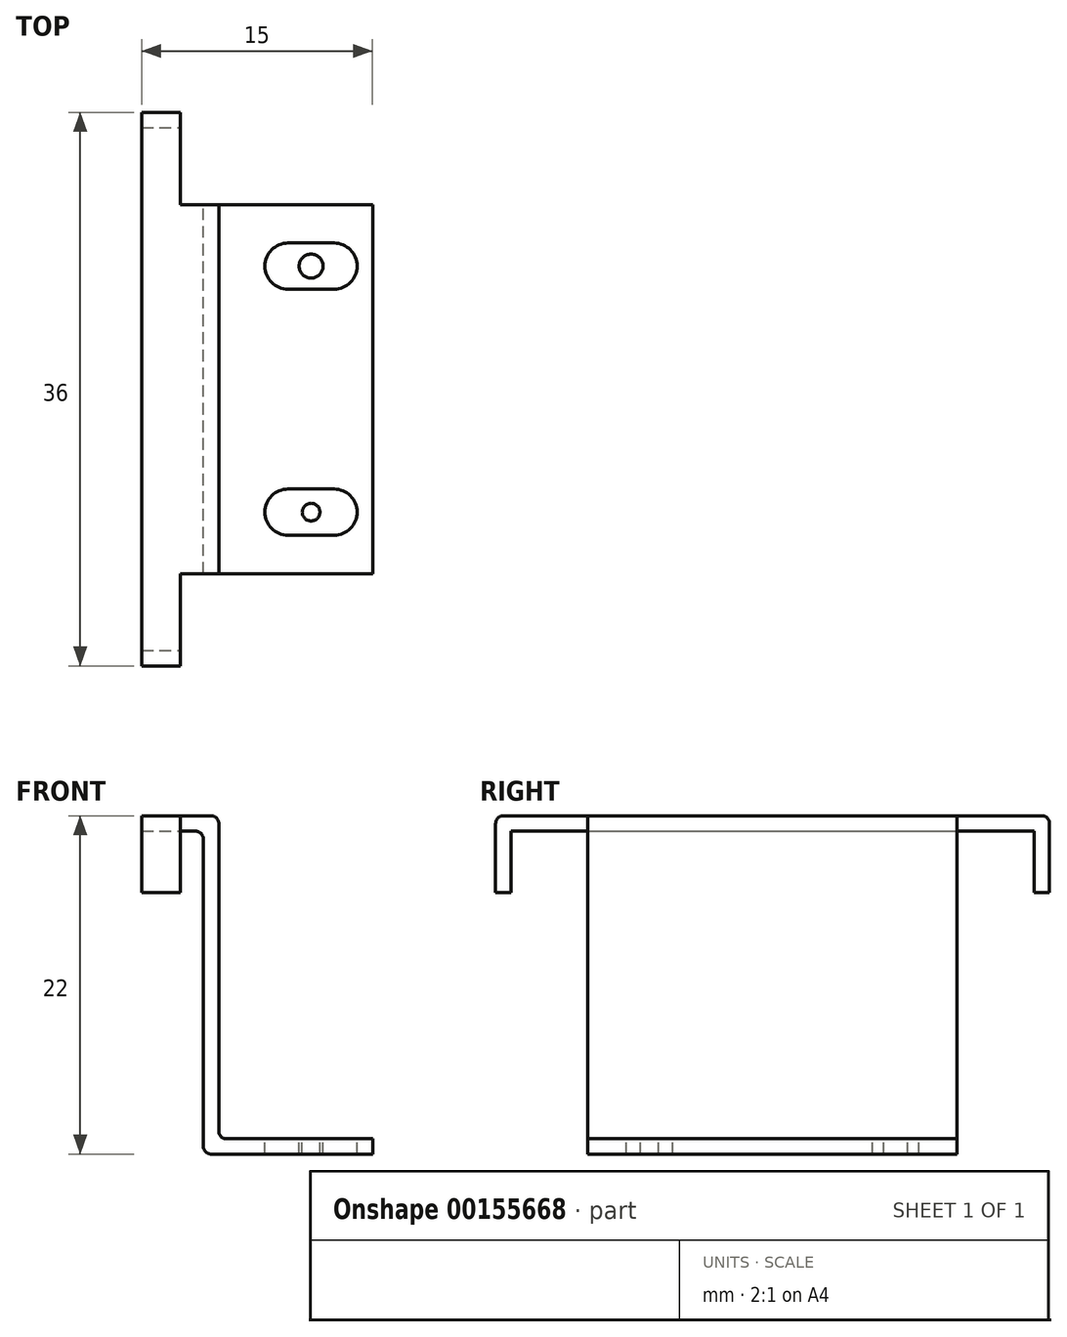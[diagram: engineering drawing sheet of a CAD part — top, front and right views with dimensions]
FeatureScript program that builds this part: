
annotation { "Feature Type Name" : "Feature", "Feature Type Description" : "" }
export const myFeature = defineFeature(function(context is Context, id is Id, definition is map)
    precondition{}
    {
        {
            var Q0;
            Q0=qCreatedBy(makeId("Front.planeOp"),FACE);
            var sketch = newSketch(context, id + "F0", { "sketchPlane" : qUnion([Q0])});
            skLineSegment(sketch, "E0.bottom", {"start": v(47.04, 40.35) * mm, "end": v(57.04, 40.35) * mm});
            skLineSegment(sketch, "E0.top", {"start": v(46.04, 39.35) * mm, "end": v(57.04, 39.35) * mm});
            skLineSegment(sketch, "E0.right", {"start": v(57.04, 40.35) * mm, "end": v(57.04, 39.35) * mm});
            skLineSegment(sketch, "E1.left", {"start": v(47.04, 40.35) * mm, "end": v(47.04, 61.35) * mm});
            skLineSegment(sketch, "E1.right", {"start": v(46.04, 39.35) * mm, "end": v(46.04, 60.35) * mm});
            skLineSegment(sketch, "E2.bottom", {"start": v(46.04, 60.35) * mm, "end": v(42.04, 60.35) * mm});
            skLineSegment(sketch, "E2.top", {"start": v(47.04, 61.35) * mm, "end": v(42.04, 61.35) * mm});
            skLineSegment(sketch, "E2.right", {"start": v(42.04, 60.35) * mm, "end": v(42.04, 61.35) * mm});
            skSolve(sketch);
        }
        {
            var Q0;
            Q0 = qSketchRegion(id + "F0", true);
            extrude(context, id + "F1", {"entities" : qUnion([Q0]), "depth" : 24 * mm});
        }
        {
            var Q0;
            Q0=makeQuery(id+"F1.opExtrude","SWEPT_FACE",FACE,{"disambiguationData":[OSD([sQuery(id+"F0.wireOp",EDGE,"E2.top")])]});
            var sketch = newSketch(context, id + "F2", { "sketchPlane" : qUnion([Q0])});
            skPoint(sketch, "E3.oppositeSnap0", {"position": v(44.54, -24) * mm});
            skLineSegment(sketch, "E3.bottom", {"start": v(42.04, -24) * mm, "end": v(44.54, -24) * mm});
            skLineSegment(sketch, "E3.top", {"start": v(42.04, -30) * mm, "end": v(44.54, -30) * mm});
            skLineSegment(sketch, "E3.left", {"start": v(42.04, -24) * mm, "end": v(42.04, -30) * mm});
            skLineSegment(sketch, "E3.right", {"start": v(44.54, -24) * mm, "end": v(44.54, -30) * mm});
            skPoint(sketch, "E4.oppositeSnap0", {"position": v(44.54, 0) * mm});
            skLineSegment(sketch, "E4.bottom", {"start": v(42.04, 0) * mm, "end": v(44.54, 0) * mm});
            skLineSegment(sketch, "E4.top", {"start": v(42.04, 6) * mm, "end": v(44.54, 6) * mm});
            skLineSegment(sketch, "E4.left", {"start": v(42.04, 0) * mm, "end": v(42.04, 6) * mm});
            skLineSegment(sketch, "E4.right", {"start": v(44.54, 0) * mm, "end": v(44.54, 6) * mm});
            skSolve(sketch);
        }
        {
            var Q0;
            Q0 = qSketchRegion(id + "F2", true);
            extrude(context, id + "F3", {"entities" : qUnion([Q0]), "operationType" : NewBodyOperationType.ADD, "oppositeDirection" : true, "depth" : 1 * mm});
        }
        {
            var Q0;
            Q0=makeQuery(id+"F3.boolean.opBoolean","MERGE",FACE,{"derivedFrom":[makeQuery(id+"F1.opExtrude","SWEPT_FACE",FACE,{"disambiguationData":[OSD([sQuery(id+"F0.wireOp",EDGE,"E2.bottom")])]}),makeQuery(id+"F3.opExtrude","CAP_FACE",FACE,{"disambiguationData":[OSD([sQuery(id+"F2.wireOp",EDGE,"E3.bottom"),sQuery(id+"F2.wireOp",EDGE,"E3.top"),sQuery(id+"F2.wireOp",EDGE,"E3.left"),sQuery(id+"F2.wireOp",EDGE,"E3.right")])],"isStart":false}),makeQuery(id+"F3.opExtrude","CAP_FACE",FACE,{"disambiguationData":[OSD([sQuery(id+"F2.wireOp",EDGE,"E4.bottom"),sQuery(id+"F2.wireOp",EDGE,"E4.top"),sQuery(id+"F2.wireOp",EDGE,"E4.left"),sQuery(id+"F2.wireOp",EDGE,"E4.right")])],"isStart":false})]});
            var sketch = newSketch(context, id + "F4", { "sketchPlane" : qUnion([Q0])});
            skLineSegment(sketch, "E5.bottom", {"start": v(42.04, -6) * mm, "end": v(44.54, -6) * mm});
            skLineSegment(sketch, "E5.top", {"start": v(42.04, -5) * mm, "end": v(44.54, -5) * mm});
            skLineSegment(sketch, "E5.left", {"start": v(42.04, -6) * mm, "end": v(42.04, -5) * mm});
            skLineSegment(sketch, "E5.right", {"start": v(44.54, -6) * mm, "end": v(44.54, -5) * mm});
            skLineSegment(sketch, "E6.bottom", {"start": v(42.04, 30) * mm, "end": v(44.54, 30) * mm});
            skLineSegment(sketch, "E6.top", {"start": v(42.04, 29) * mm, "end": v(44.54, 29) * mm});
            skLineSegment(sketch, "E6.left", {"start": v(42.04, 30) * mm, "end": v(42.04, 29) * mm});
            skLineSegment(sketch, "E6.right", {"start": v(44.54, 30) * mm, "end": v(44.54, 29) * mm});
            skSolve(sketch);
        }
        {
            var Q0;
            Q0 = qSketchRegion(id + "F4", true);
            extrude(context, id + "F5", {"entities" : qUnion([Q0]), "operationType" : NewBodyOperationType.ADD, "depth" : 4 * mm});
        }
        {
            var Q0;
            Q0=makeQuery(id+"F1.opExtrude","SWEPT_EDGE",EDGE,{"disambiguationData":[OSD([sQuery(id+"F0.wireOp",EDGE,"E0.bottom"),sQuery(id+"F0.wireOp",EDGE,"E1.left")])]});
            var Q1;
            Q1=makeQuery(id+"F1.opExtrude","SWEPT_EDGE",EDGE,{"disambiguationData":[OSD([sQuery(id+"F0.wireOp",EDGE,"E0.top"),sQuery(id+"F0.wireOp",EDGE,"E1.right")])]});
            var Q2;
            Q2=makeQuery(id+"F1.opExtrude","SWEPT_EDGE",EDGE,{"disambiguationData":[OSD([sQuery(id+"F0.wireOp",EDGE,"E1.left"),sQuery(id+"F0.wireOp",EDGE,"E2.top")])]});
            var Q3;
            Q3=makeQuery(id+"F1.opExtrude","SWEPT_EDGE",EDGE,{"disambiguationData":[OSD([sQuery(id+"F0.wireOp",EDGE,"E1.right"),sQuery(id+"F0.wireOp",EDGE,"E2.bottom")])]});
            var Q4;
            Q4=makeQuery(id+"F5.opExtrude","CAP_EDGE",EDGE,{"disambiguationData":[OSD([sQuery(id+"F4.wireOp",EDGE,"E5.top")])],"isStart":true});
            var Q5;
            Q5=makeQuery(id+"F5.opExtrude","CAP_EDGE",EDGE,{"disambiguationData":[OSD([sQuery(id+"F4.wireOp",EDGE,"E6.top")])],"isStart":true});
            var Q6;
            Q6=makeQuery(id+"F3.opExtrude","CAP_EDGE",EDGE,{"disambiguationData":[OSD([sQuery(id+"F2.wireOp",EDGE,"E4.top")])],"isStart":true});
            var Q7;
            Q7=makeQuery(id+"F3.opExtrude","CAP_EDGE",EDGE,{"disambiguationData":[OSD([sQuery(id+"F2.wireOp",EDGE,"E3.top")])],"isStart":true});
            fillet(context, id + "F6", {"entities" : qUnion([Q0, Q1, Q2, Q3, Q4, Q5, Q6, Q7]), "radius" : 0.5 * mm, "tangentPropagation" : true, "allowEdgeOverflow" : false});
        }
        {
            var Q0;
            Q0=makeQuery(id+"F1.opExtrude","SWEPT_FACE",FACE,{"disambiguationData":[OSD([sQuery(id+"F0.wireOp",EDGE,"E0.bottom")])]});
            var sketch = newSketch(context, id + "F7", { "sketchPlane" : qUnion([Q0])});
            skLineSegment(sketch, "E7.bottom", {"start": v(54.54, -18.5) * mm, "end": v(51.54, -18.5) * mm});
            skLineSegment(sketch, "E7.top", {"start": v(54.54, -21.5) * mm, "end": v(51.54, -21.5) * mm});
            skPoint(sketch, "E7.middle", {"position": v(53.04, -20) * mm});
            skArc(sketch, "E8", {"start": v(51.54, -21.5) * mm, "mid": v(50.04, -20) * mm, "end": v(51.54, -18.5) * mm});
            skArc(sketch, "E9", {"start": v(54.54, -21.5) * mm, "mid": v(56.04, -20) * mm, "end": v(54.54, -18.5) * mm});
            skLineSegment(sketch, "E10.bottom", {"start": v(54.54, -2.5) * mm, "end": v(51.54, -2.5) * mm});
            skLineSegment(sketch, "E10.top", {"start": v(54.54, -5.5) * mm, "end": v(51.54, -5.5) * mm});
            skPoint(sketch, "E10.middle", {"position": v(53.04, -4) * mm});
            skArc(sketch, "E11", {"start": v(51.54, -5.5) * mm, "mid": v(50.04, -4) * mm, "end": v(51.54, -2.5) * mm});
            skArc(sketch, "E12", {"start": v(54.54, -5.5) * mm, "mid": v(56.04, -4) * mm, "end": v(54.54, -2.5) * mm});
            skCircle(sketch, "E13", {"center": v(53.04, -20) * mm, "radius": 0.58 * mm});
            skCircle(sketch, "E14", {"center": v(53.04, -4) * mm, "radius": 0.78 * mm});
            skSolve(sketch);
        }
        {
            var Q0;
            Q0 = qSketchRegion(id + "F7", true);
            extrude(context, id + "F8", {"entities" : qUnion([Q0]), "operationType" : NewBodyOperationType.REMOVE, "oppositeDirection" : true, "depth" : 2 * mm});
        }
    });
